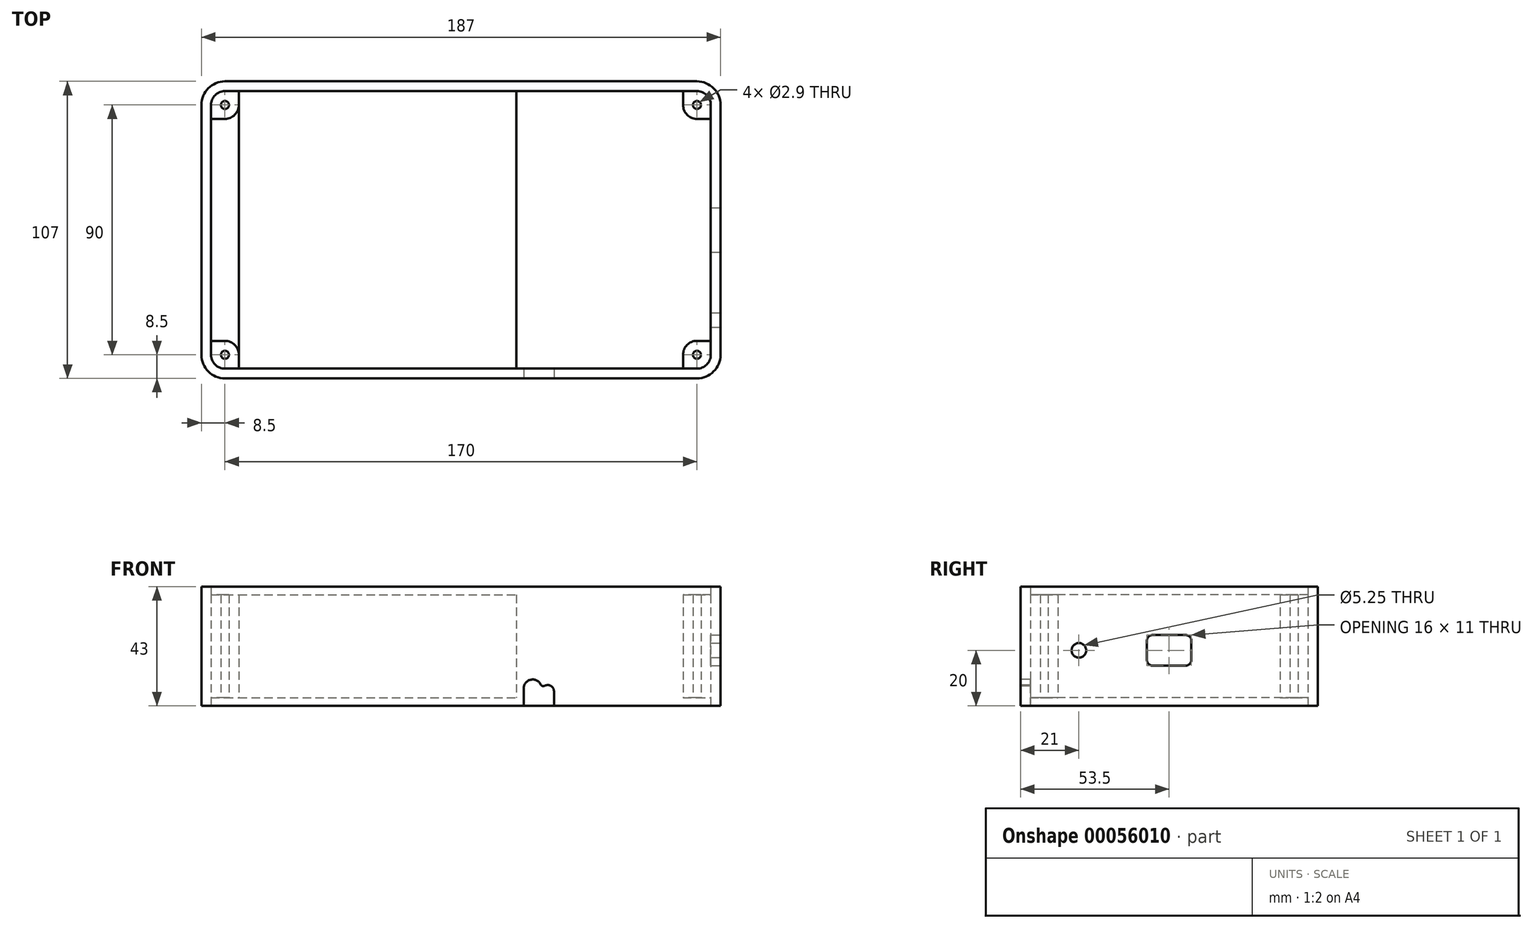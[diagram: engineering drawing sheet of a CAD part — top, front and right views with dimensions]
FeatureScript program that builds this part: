
annotation { "Feature Type Name" : "Feature", "Feature Type Description" : "" }
export const myFeature = defineFeature(function(context is Context, id is Id, definition is map)
    precondition{}
    {
        {
            var Q0;
            Q0=qCreatedBy(makeId("Top.planeOp"),FACE);
            var sketch = newSketch(context, id + "F0", { "sketchPlane" : qUnion([Q0])});
            skLineSegment(sketch, "E0.rect.bottom", {"start": v(-85, 50) * mm, "end": v(85, 50) * mm});
            skLineSegment(sketch, "E0.rect.top", {"start": v(-85, -50) * mm, "end": v(85, -50) * mm});
            skLineSegment(sketch, "E0.rect.left", {"start": v(-90, 45) * mm, "end": v(-90, -45) * mm});
            skLineSegment(sketch, "E0.rect.right", {"start": v(90, 45) * mm, "end": v(90, -45) * mm});
            skPoint(sketch, "E0.rect.middle", {"position": v(0, 0) * mm});
            skPoint(sketch, "E1.visualSharp", {"position": v(-90, 50) * mm});
            skArc(sketch, "E1.filletArc", {"start": v(-85, 50) * mm, "mid": v(-88.54, 48.54) * mm, "end": v(-90, 45) * mm});
            skPoint(sketch, "E2.visualSharp", {"position": v(-90, -50) * mm});
            skArc(sketch, "E2.filletArc", {"start": v(-90, -45) * mm, "mid": v(-88.54, -48.54) * mm, "end": v(-85, -50) * mm});
            skPoint(sketch, "E3.visualSharp", {"position": v(90, -50) * mm});
            skArc(sketch, "E3.filletArc", {"start": v(85, -50) * mm, "mid": v(88.54, -48.54) * mm, "end": v(90, -45) * mm});
            skPoint(sketch, "E4.visualSharp", {"position": v(90, 50) * mm});
            skArc(sketch, "E4.filletArc", {"start": v(90, 45) * mm, "mid": v(88.54, 48.54) * mm, "end": v(85, 50) * mm});
            skArc(sketch, "E5.0", {"start": v(93.5, 45) * mm, "mid": v(91.01, 51.01) * mm, "end": v(85, 53.5) * mm});
            skLineSegment(sketch, "E5.1", {"start": v(-85, 53.5) * mm, "end": v(85, 53.5) * mm});
            skLineSegment(sketch, "E5.2", {"start": v(93.5, 45) * mm, "end": v(93.5, -45) * mm});
            skArc(sketch, "E5.3", {"start": v(-85, 53.5) * mm, "mid": v(-91.01, 51.01) * mm, "end": v(-93.5, 45) * mm});
            skArc(sketch, "E5.4", {"start": v(85, -53.5) * mm, "mid": v(91.01, -51.01) * mm, "end": v(93.5, -45) * mm});
            skLineSegment(sketch, "E5.5", {"start": v(-85, -53.5) * mm, "end": v(85, -53.5) * mm});
            skArc(sketch, "E5.6", {"start": v(-93.5, -45) * mm, "mid": v(-91.01, -51.01) * mm, "end": v(-85, -53.5) * mm});
            skLineSegment(sketch, "E5.7", {"start": v(-93.5, 45) * mm, "end": v(-93.5, -45) * mm});
            skSolve(sketch);
        }
        {
            var Q0;
            Q0=makeQuery(id+"F0.imprint","IMPRINT",FACE,{"disambiguationData":[TD([[makeQuery(id+"F0.imprint","IMPRINT",EDGE,{"derivedFrom":sQuery(id+"F0.wireOp",EDGE,"E0.rect.bottom")}),1.0]])]});
            extrude(context, id + "F1", {"entities" : qUnion([Q0]), "depth" : 43 * mm});
        }
        {
            var Q0;
            Q0=qCreatedBy(makeId("Top.planeOp"),FACE);
            cPlane(context, id + "F2", {"entities" : qUnion([Q0]), "cplaneType" : CPlaneType.OFFSET, "offset" : 3 * mm, "width" : 150 * mm, "height" : 150 * mm});
        }
        {
            var Q0;
            Q0=qCreatedBy(id+"F2.planeOp",FACE);
            var sketch = newSketch(context, id + "F3", { "sketchPlane" : qUnion([Q0])});
            skLineSegment(sketch, "E6", {"start": v(0, 50) * mm, "end": v(0, -50) * mm, "construction": true});
            skLineSegment(sketch, "E7", {"start": v(-90, 0) * mm, "end": v(90, 0) * mm, "construction": true});
            skLineSegment(sketch, "E8", {"start": v(-80, 50) * mm, "end": v(-80, 45) * mm});
            skLineSegment(sketch, "E9", {"start": v(-85, 40) * mm, "end": v(-90, 40) * mm});
            skCircle(sketch, "E10", {"center": v(-85, 45) * mm, "radius": 1.45 * mm});
            skPoint(sketch, "E11.visualSharp", {"position": v(-80, 40) * mm});
            skArc(sketch, "E11.filletArc", {"start": v(-85, 40) * mm, "mid": v(-81.46, 41.46) * mm, "end": v(-80, 45) * mm});
            skArc(sketch, "E12.0", {"start": v(-85, 50) * mm, "mid": v(-88.54, 48.54) * mm, "end": v(-90, 45) * mm});
            skLineSegment(sketch, "E13", {"start": v(-85, 50) * mm, "end": v(-80, 50) * mm});
            skLineSegment(sketch, "E14", {"start": v(-90, 45) * mm, "end": v(-90, 40) * mm});
            skArc(sketch, "E15.MirrorCS", {"start": v(85, 50) * mm, "mid": v(88.54, 48.54) * mm, "end": v(90, 45) * mm});
            skArc(sketch, "E16.MirrorCS", {"start": v(85, 40) * mm, "mid": v(81.46, 41.46) * mm, "end": v(80, 45) * mm});
            skLineSegment(sketch, "E17.MirrorCS", {"start": v(85, 50) * mm, "end": v(80, 50) * mm});
            skCircle(sketch, "E18.MirrorC", {"center": v(85, 45) * mm, "radius": 1.45 * mm});
            skLineSegment(sketch, "E19.MirrorCS", {"start": v(85, 40) * mm, "end": v(90, 40) * mm});
            skLineSegment(sketch, "E20.MirrorCS", {"start": v(80, 50) * mm, "end": v(80, 45) * mm});
            skLineSegment(sketch, "E21.MirrorCS", {"start": v(90, 45) * mm, "end": v(90, 40) * mm});
            skPoint(sketch, "E22.MirrorP", {"position": v(80, 40) * mm});
            skLineSegment(sketch, "E23.MirrorCS", {"start": v(80, -50) * mm, "end": v(80, -45) * mm});
            skCircle(sketch, "E24.MirrorC", {"center": v(85, -45) * mm, "radius": 1.45 * mm});
            skArc(sketch, "E25.MirrorCS", {"start": v(85, -40) * mm, "mid": v(81.46, -41.46) * mm, "end": v(80, -45) * mm});
            skArc(sketch, "E26.MirrorCS", {"start": v(-85, -40) * mm, "mid": v(-81.46, -41.46) * mm, "end": v(-80, -45) * mm});
            skArc(sketch, "E27.MirrorCS", {"start": v(-85, -50) * mm, "mid": v(-88.54, -48.54) * mm, "end": v(-90, -45) * mm});
            skCircle(sketch, "E28.MirrorC", {"center": v(-85, -45) * mm, "radius": 1.45 * mm});
            skLineSegment(sketch, "E29.MirrorCS", {"start": v(-85, -40) * mm, "end": v(-90, -40) * mm});
            skLineSegment(sketch, "E30.MirrorCS", {"start": v(-80, -50) * mm, "end": v(-80, -45) * mm});
            skLineSegment(sketch, "E31.MirrorCS", {"start": v(90, -45) * mm, "end": v(90, -40) * mm});
            skPoint(sketch, "E32.MirrorP", {"position": v(-80, -40) * mm});
            skLineSegment(sketch, "E33.MirrorCS", {"start": v(85, -40) * mm, "end": v(90, -40) * mm});
            skLineSegment(sketch, "E34.MirrorCS", {"start": v(-85, -50) * mm, "end": v(-80, -50) * mm});
            skLineSegment(sketch, "E35.MirrorCS", {"start": v(85, -50) * mm, "end": v(80, -50) * mm});
            skLineSegment(sketch, "E36.MirrorCS", {"start": v(-90, -45) * mm, "end": v(-90, -40) * mm});
            skArc(sketch, "E37.MirrorCS", {"start": v(85, -50) * mm, "mid": v(88.54, -48.54) * mm, "end": v(90, -45) * mm});
            skPoint(sketch, "E38.MirrorP", {"position": v(80, -40) * mm});
            skSolve(sketch);
        }
        {
            var Q0;
            Q0 = qSketchRegion(id + "F3", true);
            extrude(context, id + "F4", {"entities" : qUnion([Q0]), "operationType" : NewBodyOperationType.ADD, "depth" : 37 * mm});
        }
        {
            var Q0;
            Q0=makeQuery(id+"F1.opExtrude","SWEPT_FACE",FACE,{"disambiguationData":[OSD([sQuery(id+"F0.wireOp",EDGE,"E5.2")])]});
            var sketch = newSketch(context, id + "F5", { "sketchPlane" : qUnion([Q0])});
            skArc(sketch, "E39", {"start": v(-29.1, 5.25) * mm, "mid": v(-30.2, 7.19) * mm, "end": v(-32.43, 7.22) * mm, "construction": true});
            skArc(sketch, "E40", {"start": v(-33.82, 7.66) * mm, "mid": v(-37.47, 9.42) * mm, "end": v(-40, 6.25) * mm, "construction": true});
            skLineSegment(sketch, "E41.rect.bottom", {"start": v(6, 14.5) * mm, "end": v(-6, 14.5) * mm});
            skLineSegment(sketch, "E41.rect.top", {"start": v(6, 25.5) * mm, "end": v(-6, 25.5) * mm});
            skLineSegment(sketch, "E41.rect.left", {"start": v(8, 16.5) * mm, "end": v(8, 23.5) * mm});
            skLineSegment(sketch, "E41.rect.right", {"start": v(-8, 16.5) * mm, "end": v(-8, 23.5) * mm});
            skPoint(sketch, "E41.rect.middle", {"position": v(0, 20) * mm});
            skPoint(sketch, "E42.visualSharp", {"position": v(8, 25.5) * mm});
            skArc(sketch, "E42.filletArc", {"start": v(8, 23.5) * mm, "mid": v(7.41, 24.91) * mm, "end": v(6, 25.5) * mm});
            skPoint(sketch, "E43.visualSharp", {"position": v(8, 14.5) * mm});
            skArc(sketch, "E43.filletArc", {"start": v(6, 14.5) * mm, "mid": v(7.41, 15.09) * mm, "end": v(8, 16.5) * mm});
            skPoint(sketch, "E44.visualSharp", {"position": v(-8, 14.5) * mm});
            skArc(sketch, "E44.filletArc", {"start": v(-8, 16.5) * mm, "mid": v(-7.41, 15.09) * mm, "end": v(-6, 14.5) * mm});
            skPoint(sketch, "E45.visualSharp", {"position": v(-8, 25.5) * mm});
            skArc(sketch, "E45.filletArc", {"start": v(-6, 25.5) * mm, "mid": v(-7.41, 24.91) * mm, "end": v(-8, 23.5) * mm});
            skLineSegment(sketch, "E46", {"start": v(-40, 6.25) * mm, "end": v(-40, 0) * mm, "construction": true});
            skLineSegment(sketch, "E47", {"start": v(-40, 0) * mm, "end": v(-29.1, 0) * mm, "construction": true});
            skLineSegment(sketch, "E48", {"start": v(-29.1, 0) * mm, "end": v(-29.1, 5.25) * mm, "construction": true});
            skLineSegment(sketch, "E49", {"start": v(-29.1, 3) * mm, "end": v(-40, 3) * mm, "construction": true});
            skPoint(sketch, "E50.visualSharp", {"position": v(-33.55, 5.66) * mm});
            skArc(sketch, "E50.filletArc", {"start": v(-33.82, 7.66) * mm, "mid": v(-33.22, 7.14) * mm, "end": v(-32.43, 7.22) * mm, "construction": true});
            skCircle(sketch, "E51", {"center": v(-32.5, 20) * mm, "radius": 2.62 * mm});
            skSolve(sketch);
        }
        {
            var Q0;
            Q0 = qSketchRegion(id + "F5", true);
            extrude(context, id + "F6", {"entities" : qUnion([Q0]), "operationType" : NewBodyOperationType.REMOVE, "oppositeDirection" : true, "depth" : 10 * mm});
        }
        {
            var Q0;
            Q0=qCreatedBy(id+"F2.planeOp",FACE);
            var sketch = newSketch(context, id + "F7", { "sketchPlane" : qUnion([Q0])});
            skLineSegment(sketch, "E52.rect.bottom", {"start": v(-80, 50) * mm, "end": v(20, 50) * mm});
            skLineSegment(sketch, "E52.rect.top", {"start": v(-80, -50) * mm, "end": v(20, -50) * mm});
            skLineSegment(sketch, "E52.rect.left", {"start": v(-80, 50) * mm, "end": v(-80, -50) * mm});
            skLineSegment(sketch, "E52.rect.right", {"start": v(20, 50) * mm, "end": v(20, -50) * mm});
            skPoint(sketch, "E52.rect.middle", {"position": v(-30, 0) * mm});
            skSolve(sketch);
        }
        {
            var Q0;
            Q0 = qSketchRegion(id + "F7", true);
            extrude(context, id + "F8", {"entities" : qUnion([Q0]), "depth" : 37 * mm});
        }
        {
            var Q0;
            Q0=qCreatedBy(id+"F2.planeOp",FACE);
            var sketch = newSketch(context, id + "F9", { "sketchPlane" : qUnion([Q0])});
            skLineSegment(sketch, "E53.bottom", {"start": v(33.64, -31.48) * mm, "end": v(83.64, -31.48) * mm});
            skLineSegment(sketch, "E53.top", {"start": v(33.64, 38.52) * mm, "end": v(83.64, 38.52) * mm});
            skLineSegment(sketch, "E53.left", {"start": v(33.64, -31.48) * mm, "end": v(33.64, 38.52) * mm});
            skLineSegment(sketch, "E53.right", {"start": v(83.64, -31.48) * mm, "end": v(83.64, 38.52) * mm});
            skSolve(sketch);
        }
        {
            var Q0;
            Q0=makeQuery(id+"F1.opExtrude","SWEPT_FACE",FACE,{"disambiguationData":[OSD([sQuery(id+"F0.wireOp",EDGE,"E5.5")])]});
            var sketch = newSketch(context, id + "F10", { "sketchPlane" : qUnion([Q0])});
            skArc(sketch, "E54", {"start": v(28.77, 7.66) * mm, "mid": v(25.12, 9.42) * mm, "end": v(22.6, 6.25) * mm});
            skArc(sketch, "E55", {"start": v(33.5, 5.25) * mm, "mid": v(32.4, 7.19) * mm, "end": v(30.16, 7.22) * mm});
            skLineSegment(sketch, "E56", {"start": v(22.6, 6.25) * mm, "end": v(22.6, 0) * mm});
            skLineSegment(sketch, "E57", {"start": v(22.6, 0) * mm, "end": v(33.5, 0) * mm});
            skLineSegment(sketch, "E58", {"start": v(33.5, 0) * mm, "end": v(33.5, 5.25) * mm});
            skPoint(sketch, "E59.visualSharp", {"position": v(29.04, 5.66) * mm});
            skArc(sketch, "E59.filletArc", {"start": v(28.77, 7.66) * mm, "mid": v(29.37, 7.14) * mm, "end": v(30.16, 7.22) * mm});
            skSolve(sketch);
        }
        {
            var Q0;
            Q0 = qSketchRegion(id + "F10", true);
            extrude(context, id + "F11", {"entities" : qUnion([Q0]), "operationType" : NewBodyOperationType.REMOVE, "oppositeDirection" : true, "depth" : 25 * mm});
        }
    });
